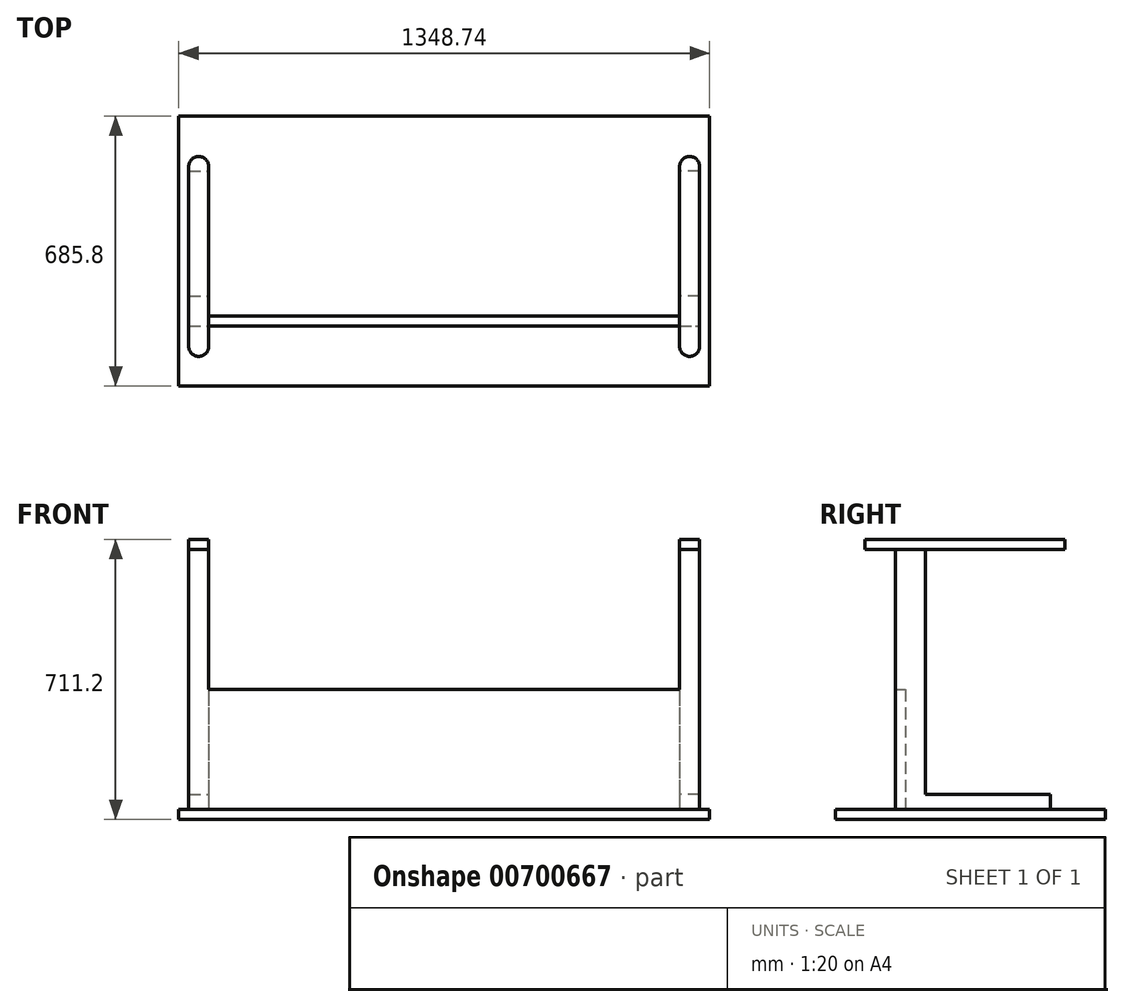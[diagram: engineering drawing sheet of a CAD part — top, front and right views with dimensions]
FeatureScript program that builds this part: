
annotation { "Feature Type Name" : "Feature", "Feature Type Description" : "" }
export const myFeature = defineFeature(function(context is Context, id is Id, definition is map)
    precondition{}
    {
        {
            var Q0;
            Q0=qCreatedBy(makeId("Top.planeOp"),FACE);
            var sketch = newSketch(context, id + "F0", { "sketchPlane" : qUnion([Q0])});
            skLineSegment(sketch, "E0.bottom", {"start": v(674.37, -342.9) * mm, "end": v(-674.37, -342.9) * mm});
            skLineSegment(sketch, "E0.top", {"start": v(674.37, 342.9) * mm, "end": v(-674.37, 342.9) * mm});
            skLineSegment(sketch, "E0.left", {"start": v(674.37, -342.9) * mm, "end": v(674.37, 342.9) * mm});
            skLineSegment(sketch, "E0.right", {"start": v(-674.37, -342.9) * mm, "end": v(-674.37, 342.9) * mm});
            skPoint(sketch, "E0.middle", {"position": v(0, 0) * mm});
            skLineSegment(sketch, "E1", {"start": v(-674.37, 342.9) * mm, "end": v(-674.37, -114.3) * mm});
            skSolve(sketch);
        }
        {
            var Q0;
            Q0=makeQuery(id+"F0.imprint","IMPRINT",FACE,{"disambiguationData":[TD([[makeQuery(id+"F0.imprint","IMPRINT",EDGE,{"derivedFrom":sQuery(id+"F0.wireOp",EDGE,"E0.bottom")}),-1.0]])]});
            extrude(context, id + "F1", {"entities" : qUnion([Q0]), "depth" : 25.4 * mm, "offsetDistance" : 25.4 * mm});
        }
        {
            var Q0;
            Q0=makeQuery(id+"F1.opExtrude","CAP_FACE",FACE,{"disambiguationData":[OSD([sQuery(id+"F0.wireOp",EDGE,"E0.bottom"),sQuery(id+"F0.wireOp",EDGE,"E0.top"),sQuery(id+"F0.wireOp",EDGE,"E0.left"),sQuery(id+"F0.wireOp",EDGE,"E0.right"),sQuery(id+"F0.wireOp",EDGE,"E1")])],"isStart":false});
            var sketch = newSketch(context, id + "F2", { "sketchPlane" : qUnion([Q0])});
            skLineSegment(sketch, "E2", {"start": v(-674.37, 342.9) * mm, "end": v(-674.37, -114.3) * mm});
            skLineSegment(sketch, "E3", {"start": v(-674.37, -114.3) * mm, "end": v(-648.97, -114.3) * mm});
            skLineSegment(sketch, "E4", {"start": v(-648.97, -114.3) * mm, "end": v(-648.97, 203.2) * mm});
            skLineSegment(sketch, "E5.bottom", {"start": v(-648.97, -114.3) * mm, "end": v(-598.17, -114.3) * mm});
            skLineSegment(sketch, "E5.top", {"start": v(-648.97, 203.2) * mm, "end": v(-598.17, 203.2) * mm});
            skLineSegment(sketch, "E5.right", {"start": v(-598.17, -114.3) * mm, "end": v(-598.17, 203.2) * mm});
            skLineSegment(sketch, "E6", {"start": v(0, -342.9) * mm, "end": v(0, 342.9) * mm});
            skLineSegment(sketch, "E7.MirrorCS", {"start": v(598.17, -114.3) * mm, "end": v(598.17, 203.2) * mm});
            skLineSegment(sketch, "E8.MirrorCS", {"start": v(648.97, 203.2) * mm, "end": v(598.17, 203.2) * mm});
            skLineSegment(sketch, "E9.MirrorCS", {"start": v(648.97, -114.3) * mm, "end": v(648.97, 203.2) * mm});
            skLineSegment(sketch, "E10.MirrorCS", {"start": v(648.97, -114.3) * mm, "end": v(598.17, -114.3) * mm});
            skSolve(sketch);
        }
        {
            var Q0;
            Q0=makeQuery(id+"F2.imprint","IMPRINT",FACE,{"disambiguationData":[TD([[makeQuery(id+"F2.imprint","IMPRINT",EDGE,{"derivedFrom":sQuery(id+"F2.wireOp",EDGE,"E5.bottom")}),1.0]])]});
            var Q1;
            Q1=makeQuery(id+"F2.imprint","IMPRINT",FACE,{"disambiguationData":[TD([[makeQuery(id+"F2.imprint","IMPRINT",EDGE,{"derivedFrom":sQuery(id+"F2.wireOp",EDGE,"E7.MirrorCS")}),-1.0]])]});
            extrude(context, id + "F3", {"entities" : qUnion([Q0, Q1]), "operationType" : NewBodyOperationType.ADD, "depth" : 38.1 * mm, "offsetDistance" : 25.4 * mm});
        }
        {
            var Q0;
            Q0=makeQuery(id+"F1.opExtrude","CAP_FACE",FACE,{"disambiguationData":[OSD([sQuery(id+"F0.wireOp",EDGE,"E0.bottom"),sQuery(id+"F0.wireOp",EDGE,"E0.top"),sQuery(id+"F0.wireOp",EDGE,"E0.left"),sQuery(id+"F0.wireOp",EDGE,"E0.right"),sQuery(id+"F0.wireOp",EDGE,"E1")])],"isStart":false});
            var sketch = newSketch(context, id + "F4", { "sketchPlane" : qUnion([Q0])});
            skLineSegment(sketch, "E11.bottom", {"start": v(-648.97, -114.3) * mm, "end": v(-598.17, -114.3) * mm});
            skLineSegment(sketch, "E11.top", {"start": v(-648.97, -190.5) * mm, "end": v(-598.17, -190.5) * mm});
            skLineSegment(sketch, "E11.left", {"start": v(-648.97, -114.3) * mm, "end": v(-648.97, -190.5) * mm});
            skLineSegment(sketch, "E11.right", {"start": v(-598.17, -114.3) * mm, "end": v(-598.17, -190.5) * mm});
            skLineSegment(sketch, "E12.bottom", {"start": v(598.17, -114.3) * mm, "end": v(648.97, -114.3) * mm});
            skLineSegment(sketch, "E12.top", {"start": v(598.17, -190.5) * mm, "end": v(648.97, -190.5) * mm});
            skLineSegment(sketch, "E12.left", {"start": v(598.17, -114.3) * mm, "end": v(598.17, -190.5) * mm});
            skLineSegment(sketch, "E12.right", {"start": v(648.97, -114.3) * mm, "end": v(648.97, -190.5) * mm});
            skSolve(sketch);
        }
        {
            var Q0;
            Q0=makeQuery(id+"F4.imprint","IMPRINT",FACE,{"disambiguationData":[TD([[makeQuery(id+"F4.imprint","IMPRINT",EDGE,{"derivedFrom":sQuery(id+"F4.wireOp",EDGE,"E11.bottom")}),-1.0]])]});
            var Q1;
            Q1 = qSketchRegion(id + "F0cJa8k7cy4R7qg_1", true);
            var Q2;
            Q2=makeQuery(id+"F4.imprint","IMPRINT",FACE,{"disambiguationData":[TD([[makeQuery(id+"F4.imprint","IMPRINT",EDGE,{"derivedFrom":sQuery(id+"F4.wireOp",EDGE,"E12.bottom")}),1.0]])]});
            extrude(context, id + "F5", {"entities" : qUnion([Q0, Q1, Q2]), "operationType" : NewBodyOperationType.ADD, "depth" : 660.4 * mm, "offsetDistance" : 25.4 * mm});
        }
        {
            var Q0;
            Q0=makeQuery(id+"F5.opExtrude","CAP_FACE",FACE,{"disambiguationData":[OSD([sQuery(id+"F4.wireOp",EDGE,"E11.bottom"),sQuery(id+"F4.wireOp",EDGE,"E11.top"),sQuery(id+"F4.wireOp",EDGE,"E11.left"),sQuery(id+"F4.wireOp",EDGE,"E11.right")])],"isStart":false});
            var sketch = newSketch(context, id + "F6", { "sketchPlane" : qUnion([Q0])});
            skLineSegment(sketch, "E13.bottom", {"start": v(-623.69, -267.73) * mm, "end": v(-623.69, -267.73) * mm});
            skLineSegment(sketch, "E13.top", {"start": v(-623.69, 240.27) * mm, "end": v(-623.69, 240.27) * mm});
            skLineSegment(sketch, "E13.left", {"start": v(-598.29, -242.33) * mm, "end": v(-598.29, 214.87) * mm});
            skLineSegment(sketch, "E13.right", {"start": v(-649.09, -242.33) * mm, "end": v(-649.09, 214.87) * mm});
            skPoint(sketch, "E13.middle", {"position": v(-623.69, -13.73) * mm});
            skPoint(sketch, "E14.visualSharp", {"position": v(-649.09, 240.27) * mm});
            skArc(sketch, "E14.filletArc", {"start": v(-623.69, 240.27) * mm, "mid": v(-641.65, 232.83) * mm, "end": v(-649.09, 214.87) * mm});
            skPoint(sketch, "E15.visualSharp", {"position": v(-598.29, 240.27) * mm});
            skArc(sketch, "E15.filletArc", {"start": v(-598.29, 214.87) * mm, "mid": v(-605.73, 232.83) * mm, "end": v(-623.69, 240.27) * mm});
            skPoint(sketch, "E16.visualSharp", {"position": v(-598.29, -267.73) * mm});
            skArc(sketch, "E16.filletArc", {"start": v(-623.69, -267.73) * mm, "mid": v(-605.73, -260.3) * mm, "end": v(-598.29, -242.33) * mm});
            skPoint(sketch, "E17.visualSharp", {"position": v(-649.09, -267.73) * mm});
            skArc(sketch, "E17.filletArc", {"start": v(-649.09, -242.33) * mm, "mid": v(-641.65, -260.3) * mm, "end": v(-623.69, -267.73) * mm});
            skLineSegment(sketch, "E18.MirrorCS", {"start": v(649.09, -242.33) * mm, "end": v(649.09, 214.87) * mm});
            skLineSegment(sketch, "E19.MirrorCS", {"start": v(598.29, -242.33) * mm, "end": v(598.29, 214.87) * mm});
            skArc(sketch, "E20.MirrorCS", {"start": v(598.29, 214.87) * mm, "mid": v(605.73, 232.83) * mm, "end": v(623.69, 240.27) * mm});
            skPoint(sketch, "E21.MirrorP", {"position": v(649.09, 240.27) * mm});
            skArc(sketch, "E22.MirrorCS", {"start": v(623.69, 240.27) * mm, "mid": v(641.65, 232.83) * mm, "end": v(649.09, 214.87) * mm});
            skArc(sketch, "E23.MirrorCS", {"start": v(649.09, -242.33) * mm, "mid": v(641.65, -260.3) * mm, "end": v(623.69, -267.73) * mm});
            skArc(sketch, "E24.MirrorCS", {"start": v(623.69, -267.73) * mm, "mid": v(605.73, -260.3) * mm, "end": v(598.29, -242.33) * mm});
            skSolve(sketch);
        }
        {
            var Q0;
            Q0 = qSketchRegion(id + "F6", true);
            extrude(context, id + "F7", {"entities" : qUnion([Q0]), "operationType" : NewBodyOperationType.ADD, "depth" : 25.4 * mm, "offsetDistance" : 25.4 * mm});
        }
        {
            var Q0;
            Q0=makeQuery(id+"F1.opExtrude","CAP_FACE",FACE,{"disambiguationData":[OSD([sQuery(id+"F0.wireOp",EDGE,"E0.bottom"),sQuery(id+"F0.wireOp",EDGE,"E0.top"),sQuery(id+"F0.wireOp",EDGE,"E0.left"),sQuery(id+"F0.wireOp",EDGE,"E0.right"),sQuery(id+"F0.wireOp",EDGE,"E1")])],"isStart":false});
            var sketch = newSketch(context, id + "F8", { "sketchPlane" : qUnion([Q0])});
            skLineSegment(sketch, "E25.bottom", {"start": v(-598.17, -190.5) * mm, "end": v(598.17, -190.5) * mm});
            skLineSegment(sketch, "E25.top", {"start": v(-598.17, -165.1) * mm, "end": v(598.17, -165.1) * mm});
            skLineSegment(sketch, "E25.left", {"start": v(-598.17, -190.5) * mm, "end": v(-598.17, -165.1) * mm});
            skLineSegment(sketch, "E25.right", {"start": v(598.17, -190.5) * mm, "end": v(598.17, -165.1) * mm});
            skSolve(sketch);
        }
        {
            var Q0;
            Q0 = qSketchRegion(id + "F8", true);
            extrude(context, id + "F9", {"entities" : qUnion([Q0]), "operationType" : NewBodyOperationType.ADD, "depth" : 304.8 * mm, "offsetDistance" : 25.4 * mm});
        }
    });
